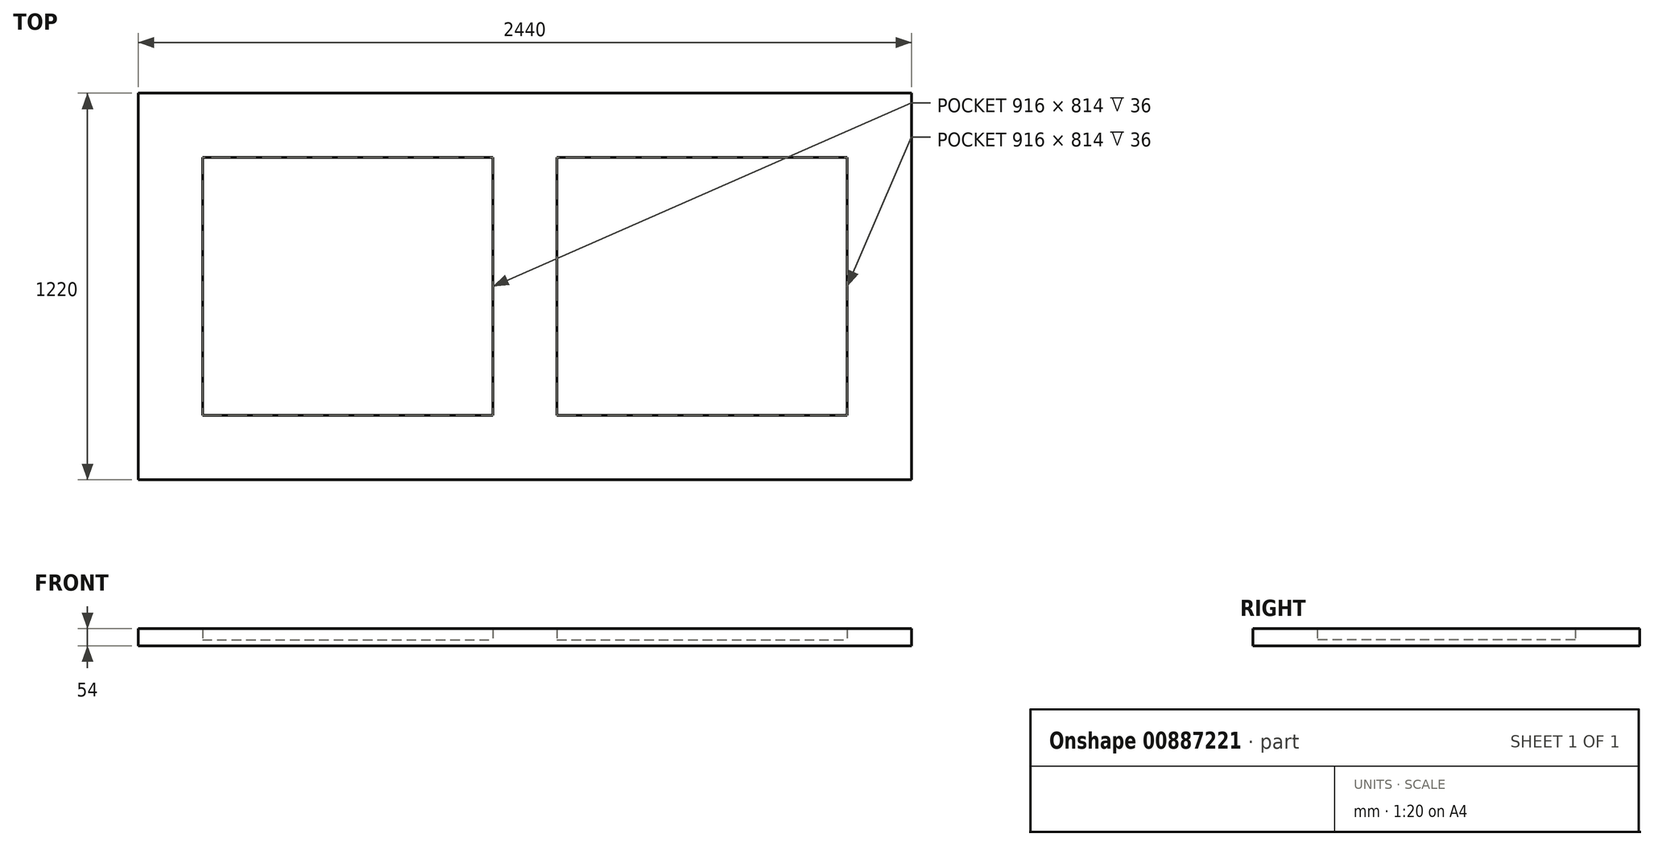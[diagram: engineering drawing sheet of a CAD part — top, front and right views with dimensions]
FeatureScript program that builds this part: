
annotation { "Feature Type Name" : "Feature", "Feature Type Description" : "" }
export const myFeature = defineFeature(function(context is Context, id is Id, definition is map)
    precondition{}
    {
        {
            var Q0;
            Q0=qCreatedBy(makeId("Top.planeOp"),FACE);
            var sketch = newSketch(context, id + "F0", { "sketchPlane" : qUnion([Q0])});
            skLineSegment(sketch, "E0", {"start": v(0, 0) * mm, "end": v(-2440, 0) * mm});
            skLineSegment(sketch, "E1", {"start": v(-2440, 0) * mm, "end": v(-2440, 1220) * mm});
            skLineSegment(sketch, "E2", {"start": v(-2440, 1220) * mm, "end": v(0, 1220) * mm});
            skLineSegment(sketch, "E3", {"start": v(0, 1220) * mm, "end": v(0, 0) * mm});
            skLineSegment(sketch, "E4.bottom", {"start": v(-2237, 1017) * mm, "end": v(-203, 1017) * mm});
            skLineSegment(sketch, "E4.top", {"start": v(-2237, 203) * mm, "end": v(-203, 203) * mm});
            skLineSegment(sketch, "E4.left", {"start": v(-2237, 1017) * mm, "end": v(-2237, 203) * mm});
            skLineSegment(sketch, "E4.right", {"start": v(-203, 1017) * mm, "end": v(-203, 203) * mm});
            skLineSegment(sketch, "E5", {"start": v(-1321, 1017) * mm, "end": v(-1321, 203) * mm});
            skLineSegment(sketch, "E6", {"start": v(-1119, 1017) * mm, "end": v(-1119, 203) * mm});
            skSolve(sketch);
        }
        {
            var Q0;
            Q0 = qSketchRegion(id + "F0", true);
            extrude(context, id + "F1", {"entities" : qUnion([Q0]), "depth" : 54 * mm, "offsetDistance" : 25 * mm});
        }
        {
            var Q0;
            {var subQ0=sQuery(id+"F0.wireOp",EDGE,"E5");Q0=makeQuery(id+"F0.imprint","IMPRINT",FACE,{"disambiguationData":[TD([[makeQuery(id+"F0.imprint","IMPRINT",EDGE,{"derivedFrom":subQ0}),1.0]])]});}
            extrude(context, id + "F2", {"entities" : qUnion([Q0]), "operationType" : NewBodyOperationType.ADD, "depth" : 54 * mm, "offsetDistance" : 25 * mm});
        }
        {
            var Q0;
            {var subQ0=sQuery(id+"F0.wireOp",EDGE,"E4.left");Q0=makeQuery(id+"F0.imprint","IMPRINT",FACE,{"disambiguationData":[TD([[makeQuery(id+"F0.imprint","IMPRINT",EDGE,{"derivedFrom":subQ0}),1.0]])]});}
            var Q1;
            {var subQ0=sQuery(id+"F0.wireOp",EDGE,"E4.right");Q1=makeQuery(id+"F0.imprint","IMPRINT",FACE,{"disambiguationData":[TD([[makeQuery(id+"F0.imprint","IMPRINT",EDGE,{"derivedFrom":subQ0}),-1.0]])]});}
            extrude(context, id + "F3", {"entities" : qUnion([Q0, Q1]), "operationType" : NewBodyOperationType.ADD, "depth" : 18 * mm, "offsetDistance" : 25 * mm});
        }
    });
